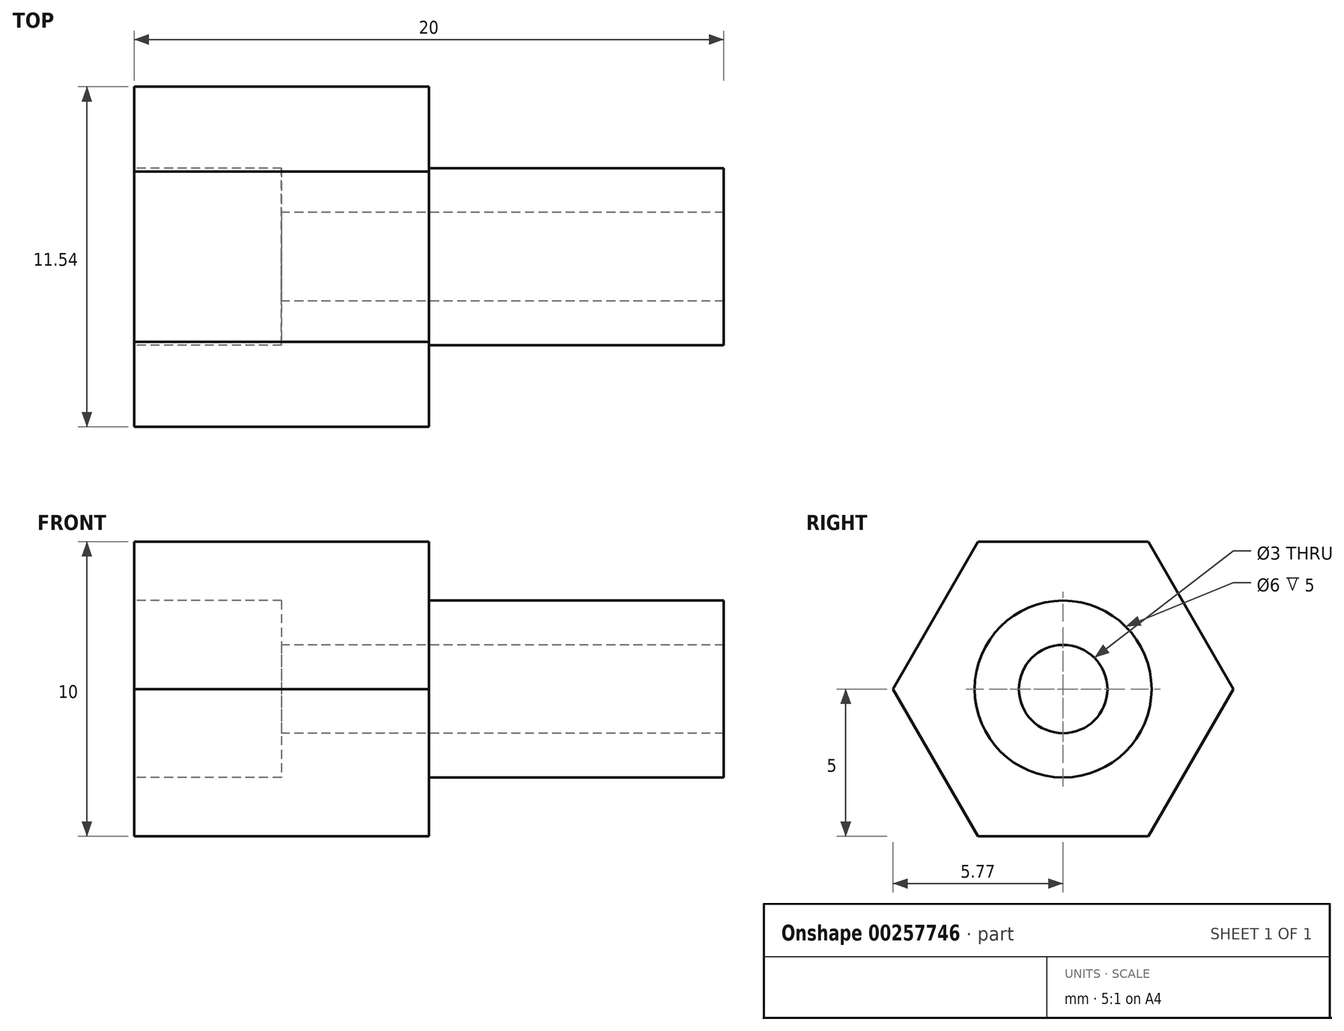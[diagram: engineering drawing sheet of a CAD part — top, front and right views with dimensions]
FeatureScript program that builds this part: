
annotation { "Feature Type Name" : "Feature", "Feature Type Description" : "" }
export const myFeature = defineFeature(function(context is Context, id is Id, definition is map)
    precondition{}
    {
        {
            var Q0;
            Q0=qCreatedBy(makeId("Right.planeOp"),FACE);
            var sketch = newSketch(context, id + "F0", { "sketchPlane" : qUnion([Q0])});
            skCircle(sketch, "E0.cCircle", {"center": v(0, 0) * mm, "radius": 5 * mm, "construction": true});
            skLineSegment(sketch, "E0.0", {"start": v(-2.89, 5) * mm, "end": v(2.89, 5) * mm});
            skLineSegment(sketch, "E0.1", {"start": v(2.89, 5) * mm, "end": v(5.77, 0) * mm});
            skLineSegment(sketch, "E0.2", {"start": v(5.77, 0) * mm, "end": v(2.89, -5) * mm});
            skLineSegment(sketch, "E0.3", {"start": v(2.89, -5) * mm, "end": v(-2.89, -5) * mm});
            skLineSegment(sketch, "E0.4", {"start": v(-2.89, -5) * mm, "end": v(-5.77, 0) * mm});
            skLineSegment(sketch, "E0.5", {"start": v(-5.77, 0) * mm, "end": v(-2.89, 5) * mm});
            skPoint(sketch, "E0.0.midPoint", {"position": v(0, 5) * mm});
            skSolve(sketch);
        }
        {
            var Q0;
            Q0=makeQuery(id+"F0.imprint","IMPRINT",FACE,{"disambiguationData":[TD([[makeQuery(id+"F0.imprint","IMPRINT",EDGE,{"derivedFrom":sQuery(id+"F0.wireOp",EDGE,"E0.0")}),-1.0]])]});
            extrude(context, id + "F1", {"entities" : qUnion([Q0]), "depth" : 10 * mm});
        }
        {
            var Q0;
            Q0=makeQuery(id+"F1.opExtrude","CAP_FACE",FACE,{"disambiguationData":[OSD([sQuery(id+"F0.wireOp",EDGE,"E0.0"),sQuery(id+"F0.wireOp",EDGE,"E0.1"),sQuery(id+"F0.wireOp",EDGE,"E0.2"),sQuery(id+"F0.wireOp",EDGE,"E0.3"),sQuery(id+"F0.wireOp",EDGE,"E0.4"),sQuery(id+"F0.wireOp",EDGE,"E0.5")])],"isStart":false});
            var sketch = newSketch(context, id + "F2", { "sketchPlane" : qUnion([Q0])});
            skCircle(sketch, "E1", {"center": v(0, 0) * mm, "radius": 3 * mm});
            skSolve(sketch);
        }
        {
            var Q0;
            Q0=makeQuery(id+"F2.imprint","IMPRINT",FACE,{"disambiguationData":[TD([[makeQuery(id+"F2.imprint","IMPRINT",EDGE,{"derivedFrom":sQuery(id+"F2.wireOp",EDGE,"E1")}),1.0]])]});
            var Q1;
            Q1=sQuery(id+"F2.wireOp",EDGE,"E1");
            extrude(context, id + "F3", {"entities" : qUnion([Q0]), "operationType" : NewBodyOperationType.ADD, "surfaceEntities" : qUnion([Q1]), "depth" : 10 * mm});
        }
        {
            var Q0;
            Q0=makeQuery(id+"F1.opExtrude","CAP_FACE",FACE,{"disambiguationData":[OSD([sQuery(id+"F0.wireOp",EDGE,"E0.0"),sQuery(id+"F0.wireOp",EDGE,"E0.1"),sQuery(id+"F0.wireOp",EDGE,"E0.2"),sQuery(id+"F0.wireOp",EDGE,"E0.3"),sQuery(id+"F0.wireOp",EDGE,"E0.4"),sQuery(id+"F0.wireOp",EDGE,"E0.5")])],"isStart":true});
            var sketch = newSketch(context, id + "F4", { "sketchPlane" : qUnion([Q0])});
            skCircle(sketch, "E2", {"center": v(0, 0) * mm, "radius": 1.5 * mm});
            skSolve(sketch);
        }
        {
            var Q0;
            Q0=makeQuery(id+"F4.imprint","IMPRINT",FACE,{"disambiguationData":[TD([[makeQuery(id+"F4.imprint","IMPRINT",EDGE,{"derivedFrom":sQuery(id+"F4.wireOp",EDGE,"E2")}),1.0]])]});
            extrude(context, id + "F5", {"entities" : qUnion([Q0]), "operationType" : NewBodyOperationType.REMOVE, "oppositeDirection" : true, "depth" : 25 * mm});
        }
        {
            var Q0;
            Q0=makeQuery(id+"F1.opExtrude","CAP_FACE",FACE,{"disambiguationData":[OSD([sQuery(id+"F0.wireOp",EDGE,"E0.0"),sQuery(id+"F0.wireOp",EDGE,"E0.1"),sQuery(id+"F0.wireOp",EDGE,"E0.2"),sQuery(id+"F0.wireOp",EDGE,"E0.3"),sQuery(id+"F0.wireOp",EDGE,"E0.4"),sQuery(id+"F0.wireOp",EDGE,"E0.5")])],"isStart":true});
            var sketch = newSketch(context, id + "F6", { "sketchPlane" : qUnion([Q0])});
            skCircle(sketch, "E3", {"center": v(0, 0) * mm, "radius": 3 * mm});
            skSolve(sketch);
        }
        {
            var Q0;
            Q0=makeQuery(id+"F6.imprint","IMPRINT",FACE,{"disambiguationData":[TD([[makeQuery(id+"F6.imprint","IMPRINT",EDGE,{"derivedFrom":sQuery(id+"F6.wireOp",EDGE,"E3")}),1.0]])]});
            extrude(context, id + "F7", {"entities" : qUnion([Q0]), "operationType" : NewBodyOperationType.REMOVE, "oppositeDirection" : true, "depth" : 5 * mm});
        }
    });
